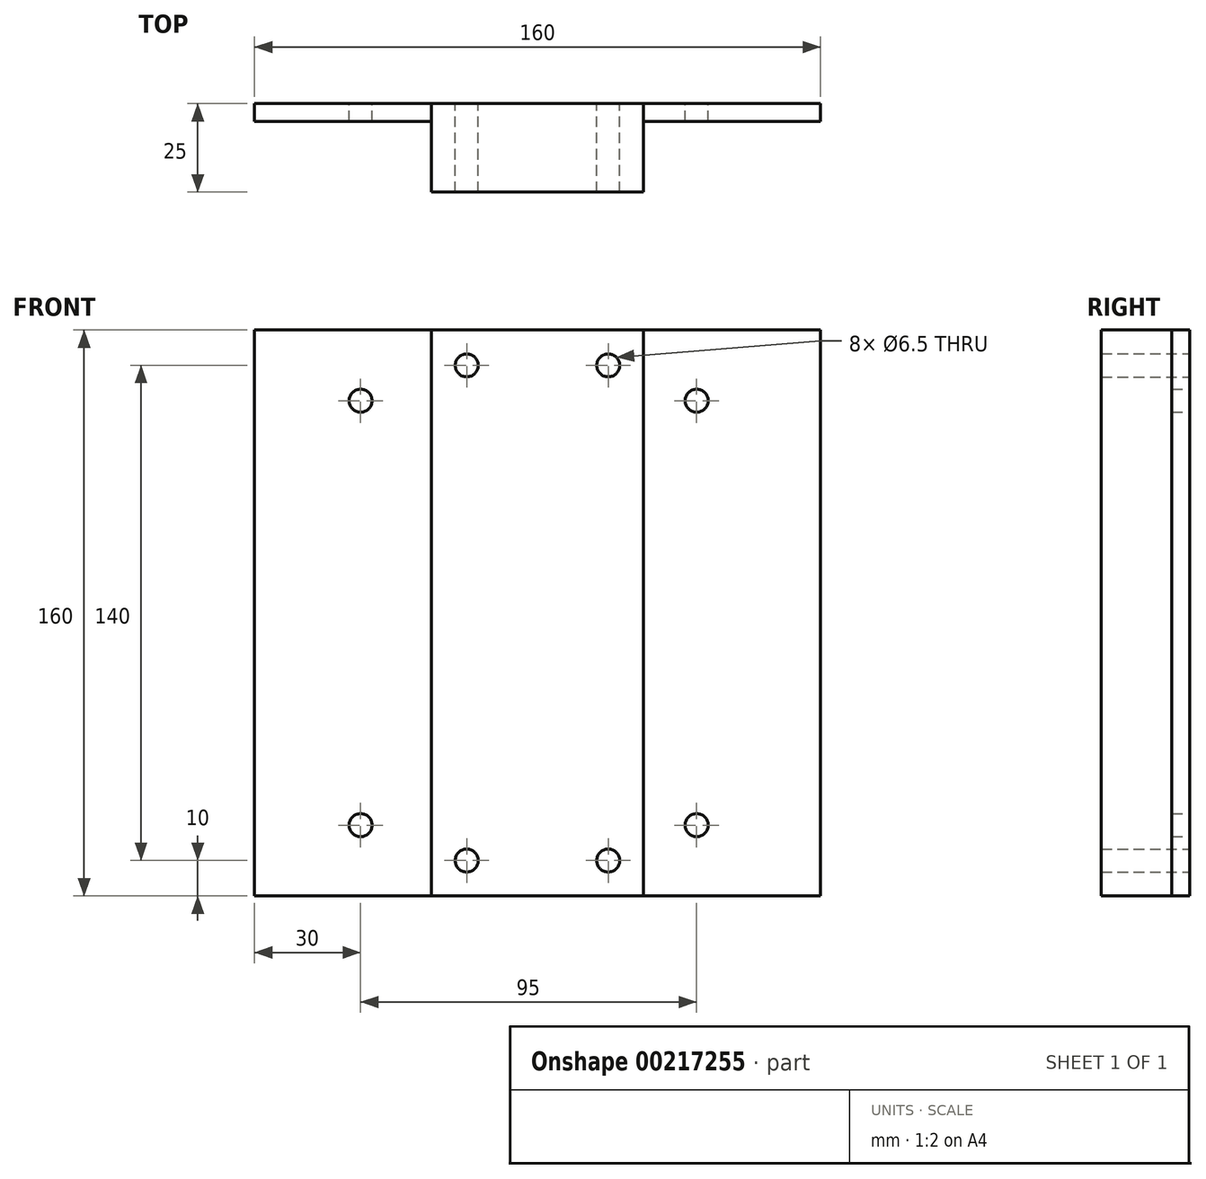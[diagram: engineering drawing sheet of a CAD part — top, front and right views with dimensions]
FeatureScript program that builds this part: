
annotation { "Feature Type Name" : "Feature", "Feature Type Description" : "" }
export const myFeature = defineFeature(function(context is Context, id is Id, definition is map)
    precondition{}
    {
        {
            var Q0;
            Q0=qCreatedBy(makeId("Front.planeOp"),FACE);
            var sketch = newSketch(context, id + "F0", { "sketchPlane" : qUnion([Q0])});
            skPoint(sketch, "E0.middle", {"position": v(0, 0) * mm});
            skLineSegment(sketch, "E1", {"start": v(-27.5, 80) * mm, "end": v(32.5, 80) * mm});
            skLineSegment(sketch, "E2", {"start": v(-27.5, -80) * mm, "end": v(32.5, -80) * mm});
            skLineSegment(sketch, "E3", {"start": v(-27.5, 80) * mm, "end": v(-27.5, -80) * mm});
            skLineSegment(sketch, "E4", {"start": v(32.5, 80) * mm, "end": v(32.5, -80) * mm});
            skLineSegment(sketch, "E5", {"start": v(-27.5, 80) * mm, "end": v(-77.5, 80) * mm});
            skLineSegment(sketch, "E6", {"start": v(-77.5, 80) * mm, "end": v(-77.5, -80) * mm});
            skLineSegment(sketch, "E7", {"start": v(-77.5, -80) * mm, "end": v(-27.5, -80) * mm});
            skLineSegment(sketch, "E8", {"start": v(32.5, -80) * mm, "end": v(82.5, -80) * mm});
            skLineSegment(sketch, "E9", {"start": v(82.5, -80) * mm, "end": v(82.5, 80) * mm});
            skLineSegment(sketch, "E10", {"start": v(82.5, 80) * mm, "end": v(32.5, 80) * mm});
            skCircle(sketch, "E11", {"center": v(-17.5, 70) * mm, "radius": 3.25 * mm});
            skCircle(sketch, "E12", {"center": v(22.5, 70) * mm, "radius": 3.25 * mm});
            skCircle(sketch, "E13", {"center": v(-47.5, 60) * mm, "radius": 3.25 * mm});
            skLineSegment(sketch, "E14", {"start": v(0, 0) * mm, "end": v(0, 8.56) * mm});
            skLineSegment(sketch, "E15", {"start": v(0, 8.56) * mm, "end": v(0, 0) * mm});
            skLineSegment(sketch, "E16", {"start": v(0, 0) * mm, "end": v(-8.92, 0) * mm});
            skCircle(sketch, "E17.MirrorC", {"center": v(47.5, 60) * mm, "radius": 3.25 * mm});
            skCircle(sketch, "E18.MirrorC", {"center": v(-17.5, -70) * mm, "radius": 3.25 * mm});
            skCircle(sketch, "E19.MirrorC", {"center": v(22.5, -70) * mm, "radius": 3.25 * mm});
            skCircle(sketch, "E20.MirrorC", {"center": v(-47.5, -60) * mm, "radius": 3.25 * mm});
            skCircle(sketch, "E21.MirrorC", {"center": v(47.5, -60) * mm, "radius": 3.25 * mm});
            skSolve(sketch);
        }
        {
            var Q0;
            {var subQ0=sQuery(id+"F0.wireOp",EDGE,"E0.top");Q0=makeQuery(id+"F0.imprint","IMPRINT",FACE,{"disambiguationData":[TD([[makeQuery(id+"F0.imprint","IMPRINT",EDGE,{"derivedFrom":subQ0}),1.0]])]});}
            var Q1;
            Q1=makeQuery(id+"F0.imprint","IMPRINT",FACE,{"disambiguationData":[TD([[makeQuery(id+"F0.imprint","IMPRINT",EDGE,{"derivedFrom":sQuery(id+"F0.wireOp",EDGE,"E3")}),-1.0]])]});
            var Q2;
            Q2=makeQuery(id+"F0.imprint","IMPRINT",FACE,{"disambiguationData":[TD([[makeQuery(id+"F0.imprint","IMPRINT",EDGE,{"derivedFrom":sQuery(id+"F0.wireOp",EDGE,"E4")}),1.0]])]});
            extrude(context, id + "F1", {"entities" : qUnion([Q0, Q1, Q2]), "depth" : 5 * mm});
        }
        {
            var Q0;
            Q0=makeQuery(id+"F0.imprint","IMPRINT",FACE,{"disambiguationData":[TD([[makeQuery(id+"F0.imprint","IMPRINT",EDGE,{"derivedFrom":sQuery(id+"F0.wireOp",EDGE,"E1")}),-1.0]])]});
            extrude(context, id + "F2", {"entities" : qUnion([Q0]), "depth" : 25 * mm});
        }
    });
